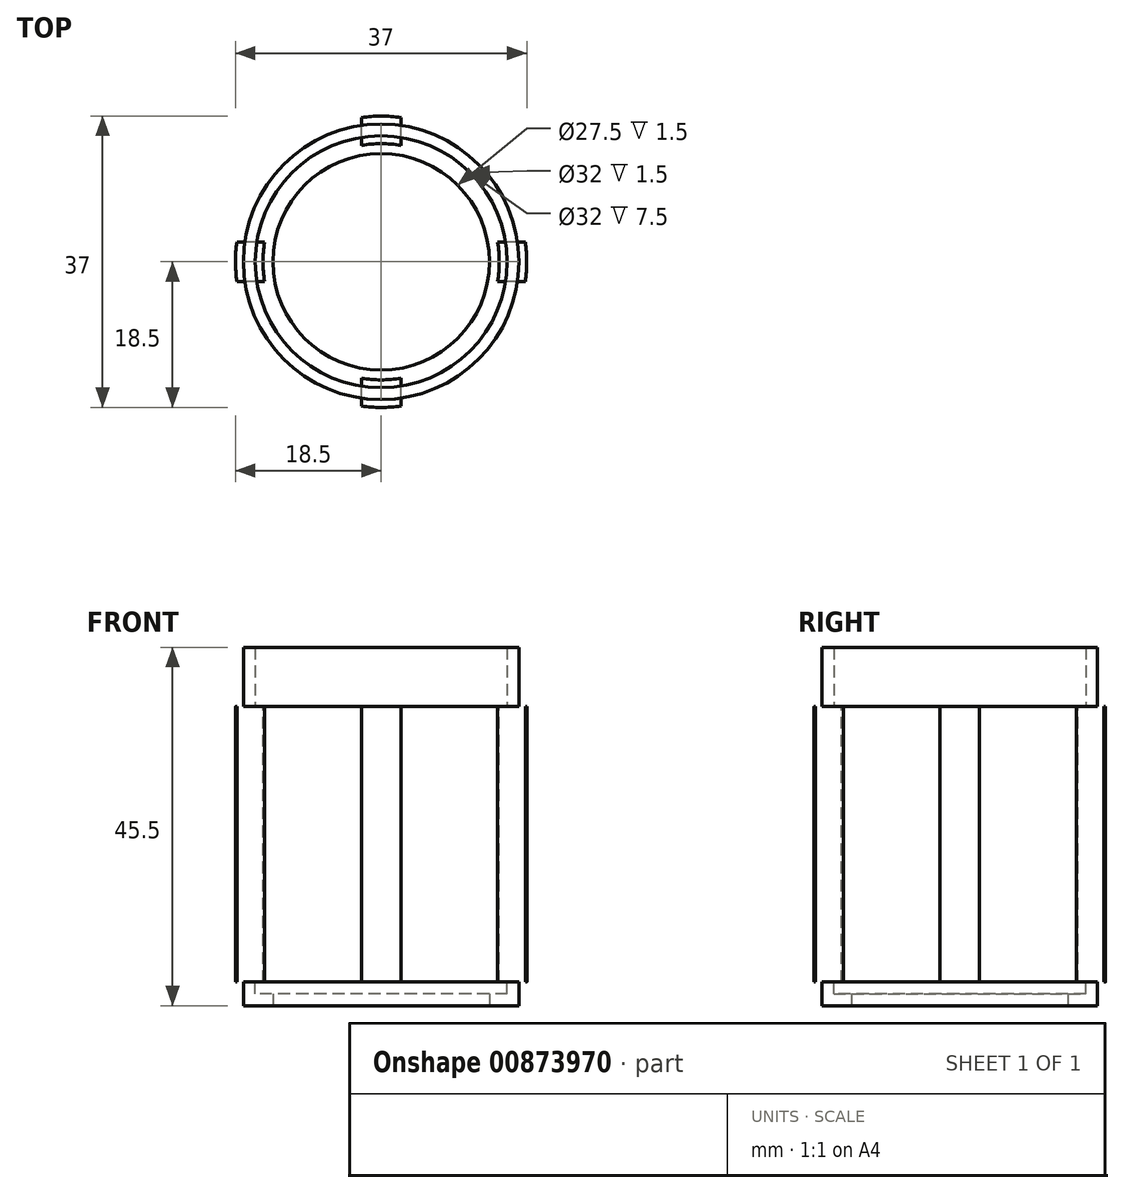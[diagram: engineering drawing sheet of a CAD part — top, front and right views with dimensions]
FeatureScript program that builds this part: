
annotation { "Feature Type Name" : "Feature", "Feature Type Description" : "" }
export const myFeature = defineFeature(function(context is Context, id is Id, definition is map)
    precondition{}
    {
        {
            var Q0;
            Q0=qCreatedBy(makeId("Top.planeOp"),FACE);
            var sketch = newSketch(context, id + "F0", { "sketchPlane" : qUnion([Q0])});
            skPoint(sketch, "E0.first.point", {"position": v(0, 0) * mm});
            skCircle(sketch, "E1", {"center": v(0, 0) * mm, "radius": 18.5 * mm});
            skCircle(sketch, "E2", {"center": v(0, 0) * mm, "radius": 13.75 * mm});
            skSolve(sketch);
        }
        {
            var Q0;
            Q0=makeQuery(id+"F0.imprint","IMPRINT",FACE,{"disambiguationData":[TD([[makeQuery(id+"F0.imprint","IMPRINT",EDGE,{"derivedFrom":sQuery(id+"F0.wireOp",EDGE,"E1")}),1.0]])]});
            extrude(context, id + "F1", {"entities" : qUnion([Q0]), "depth" : 43 * mm, "offsetDistance" : 25 * mm});
        }
        {
            var Q0;
            Q0=makeQuery(id+"F1.opExtrude","CAP_FACE",FACE,{"disambiguationData":[OSD([sQuery(id+"F0.wireOp",EDGE,"dMLi9CjI-w3AJ-lqrU-xDtC-pNT5ZKXLwRoQ"),sQuery(id+"F0.wireOp",EDGE,"p6jEfgZd-gn9l-At6D-uO4C-P7PHmhyGIQ6Y"),sQuery(id+"F0.wireOp",EDGE,"bsXDQPTp-62U9-H9b8-tNQK-BlYfqYmaa6Ta"),sQuery(id+"F0.wireOp",EDGE,"E1")])],"isStart":false});
            var sketch = newSketch(context, id + "F2", { "sketchPlane" : qUnion([Q0])});
            skCircle(sketch, "E3", {"center": v(0, 0) * mm, "radius": 15 * mm});
            skCircle(sketch, "E4", {"center": v(0, 0) * mm, "radius": 13.75 * mm});
            skSolve(sketch);
        }
        {
            var Q0;
            Q0 = qSketchRegion(id + "F2", true);
            var Q1;
            Q1 = qSketchRegion(id + "F5", true);
            extrude(context, id + "F3", {"entities" : qUnion([Q0, Q1]), "operationType" : NewBodyOperationType.REMOVE, "oppositeDirection" : true, "depth" : 41.5 * mm, "offsetDistance" : 25 * mm});
        }
        {
            var Q0;
            Q0=qCreatedBy(makeId("Top.planeOp"),FACE);
            cPlane(context, id + "F4", {"entities" : qUnion([Q0]), "cplaneType" : CPlaneType.OFFSET, "offset" : 3 * mm, "width" : 150 * mm, "height" : 150 * mm});
        }
        {
            var Q0;
            Q0=qCreatedBy(id+"F4.planeOp",FACE);
            var sketch = newSketch(context, id + "F5", { "sketchPlane" : qUnion([Q0])});
            skLineSegment(sketch, "E5.bottom", {"start": v(36.84, 2.5) * mm, "end": v(-36.84, 2.5) * mm});
            skLineSegment(sketch, "E5.top", {"start": v(36.84, -2.5) * mm, "end": v(-36.84, -2.5) * mm});
            skLineSegment(sketch, "E5.left", {"start": v(36.84, 2.5) * mm, "end": v(36.84, -2.5) * mm});
            skLineSegment(sketch, "E5.right", {"start": v(-36.84, 2.5) * mm, "end": v(-36.84, -2.5) * mm});
            skPoint(sketch, "E5.middle", {"position": v(0, 0) * mm});
            skLineSegment(sketch, "E6.bottom", {"start": v(2.5, -34.17) * mm, "end": v(-2.5, -34.17) * mm});
            skLineSegment(sketch, "E6.top", {"start": v(2.5, 34.17) * mm, "end": v(-2.5, 34.17) * mm});
            skLineSegment(sketch, "E6.left", {"start": v(2.5, -34.17) * mm, "end": v(2.5, 34.17) * mm});
            skLineSegment(sketch, "E6.right", {"start": v(-2.5, -34.17) * mm, "end": v(-2.5, 34.17) * mm});
            skSolve(sketch);
        }
        {
            var Q0;
            Q0 = qSketchRegion(id + "F5", true);
            extrude(context, id + "F6", {"entities" : qUnion([Q0]), "operationType" : NewBodyOperationType.INTERSECT, "depth" : 35 * mm, "offsetDistance" : 25 * mm});
        }
        {
            var Q0;
            Q0=qCreatedBy(makeId("Top.planeOp"),FACE);
            var sketch = newSketch(context, id + "F7", { "sketchPlane" : qUnion([Q0])});
            skCircle(sketch, "E7", {"center": v(0, 0) * mm, "radius": 17.5 * mm});
            skCircle(sketch, "E8", {"center": v(0, 0) * mm, "radius": 13.75 * mm});
            skSolve(sketch);
        }
        {
            var Q0;
            Q0 = qSketchRegion(id + "F7", true);
            extrude(context, id + "F8", {"entities" : qUnion([Q0]), "depth" : 3 * mm, "offsetDistance" : 25 * mm});
        }
        {
            var Q0;
            Q0=qCreatedBy(makeId("Top.planeOp"),FACE);
            cPlane(context, id + "F9", {"entities" : qUnion([Q0]), "cplaneType" : CPlaneType.OFFSET, "offset" : 38 * mm, "width" : 150 * mm, "height" : 150 * mm});
        }
        {
            var Q0;
            Q0=qCreatedBy(id+"F9.planeOp",FACE);
            var sketch = newSketch(context, id + "F10", { "sketchPlane" : qUnion([Q0])});
            skCircle(sketch, "E9", {"center": v(0, 0) * mm, "radius": 17.5 * mm});
            skCircle(sketch, "E10", {"center": v(0, 0) * mm, "radius": 16 * mm});
            skSolve(sketch);
        }
        {
            var Q0;
            Q0 = qSketchRegion(id + "F10", true);
            extrude(context, id + "F11", {"entities" : qUnion([Q0]), "depth" : 7.5 * mm, "offsetDistance" : 25 * mm});
        }
        {
            var Q0;
            Q0=makeQuery(id+"F8.opExtrude","CAP_FACE",FACE,{"disambiguationData":[OSD([sQuery(id+"F7.wireOp",EDGE,"E7"),sQuery(id+"F7.wireOp",EDGE,"E8")])],"isStart":false});
            var sketch = newSketch(context, id + "F12", { "sketchPlane" : qUnion([Q0])});
            skCircle(sketch, "E11", {"center": v(0, 0) * mm, "radius": 16 * mm});
            skSolve(sketch);
        }
        {
            var Q0;
            Q0 = qSketchRegion(id + "F12", true);
            extrude(context, id + "F13", {"entities" : qUnion([Q0]), "operationType" : NewBodyOperationType.REMOVE, "oppositeDirection" : true, "depth" : 1.5 * mm, "offsetDistance" : 25 * mm});
        }
    });
